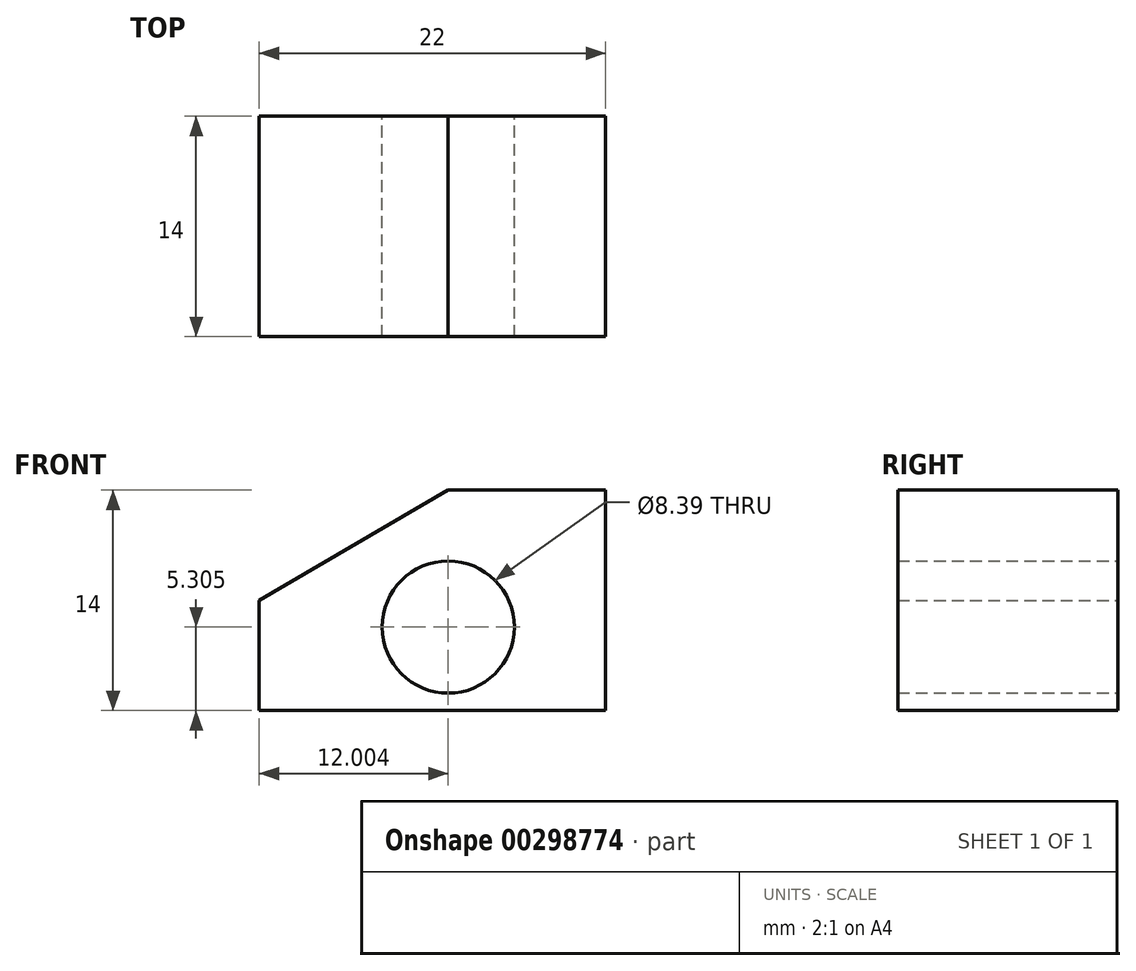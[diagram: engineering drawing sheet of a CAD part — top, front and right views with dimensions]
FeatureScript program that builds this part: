
annotation { "Feature Type Name" : "Feature", "Feature Type Description" : "" }
export const myFeature = defineFeature(function(context is Context, id is Id, definition is map)
    precondition{}
    {
        {
            var Q0;
            Q0=qCreatedBy(makeId("Front.planeOp"),FACE);
            var sketch = newSketch(context, id + "F0", { "sketchPlane" : qUnion([Q0])});
            skLineSegment(sketch, "E0", {"start": v(-55, 18.24) * mm, "end": v(-33, 18.24) * mm});
            skLineSegment(sketch, "E1", {"start": v(-33, 18.24) * mm, "end": v(-33, 32.24) * mm});
            skLineSegment(sketch, "E2", {"start": v(-33, 32.24) * mm, "end": v(-43, 32.24) * mm});
            skLineSegment(sketch, "E3", {"start": v(-55, 18.24) * mm, "end": v(-55, 25.24) * mm});
            skLineSegment(sketch, "E4", {"start": v(-43, 32.24) * mm, "end": v(-55, 25.24) * mm});
            skCircle(sketch, "E5", {"center": v(-43, 23.55) * mm, "radius": 4.2 * mm});
            skSolve(sketch);
        }
        {
            var Q0;
            Q0=makeQuery(id+"F0.imprint","IMPRINT",FACE,{"disambiguationData":[TD([[makeQuery(id+"F0.imprint","IMPRINT",EDGE,{"derivedFrom":sQuery(id+"F0.wireOp",EDGE,"E0")}),1.0]])]});
            extrude(context, id + "F1", {"entities" : qUnion([Q0]), "depth" : 14 * mm});
        }
    });
